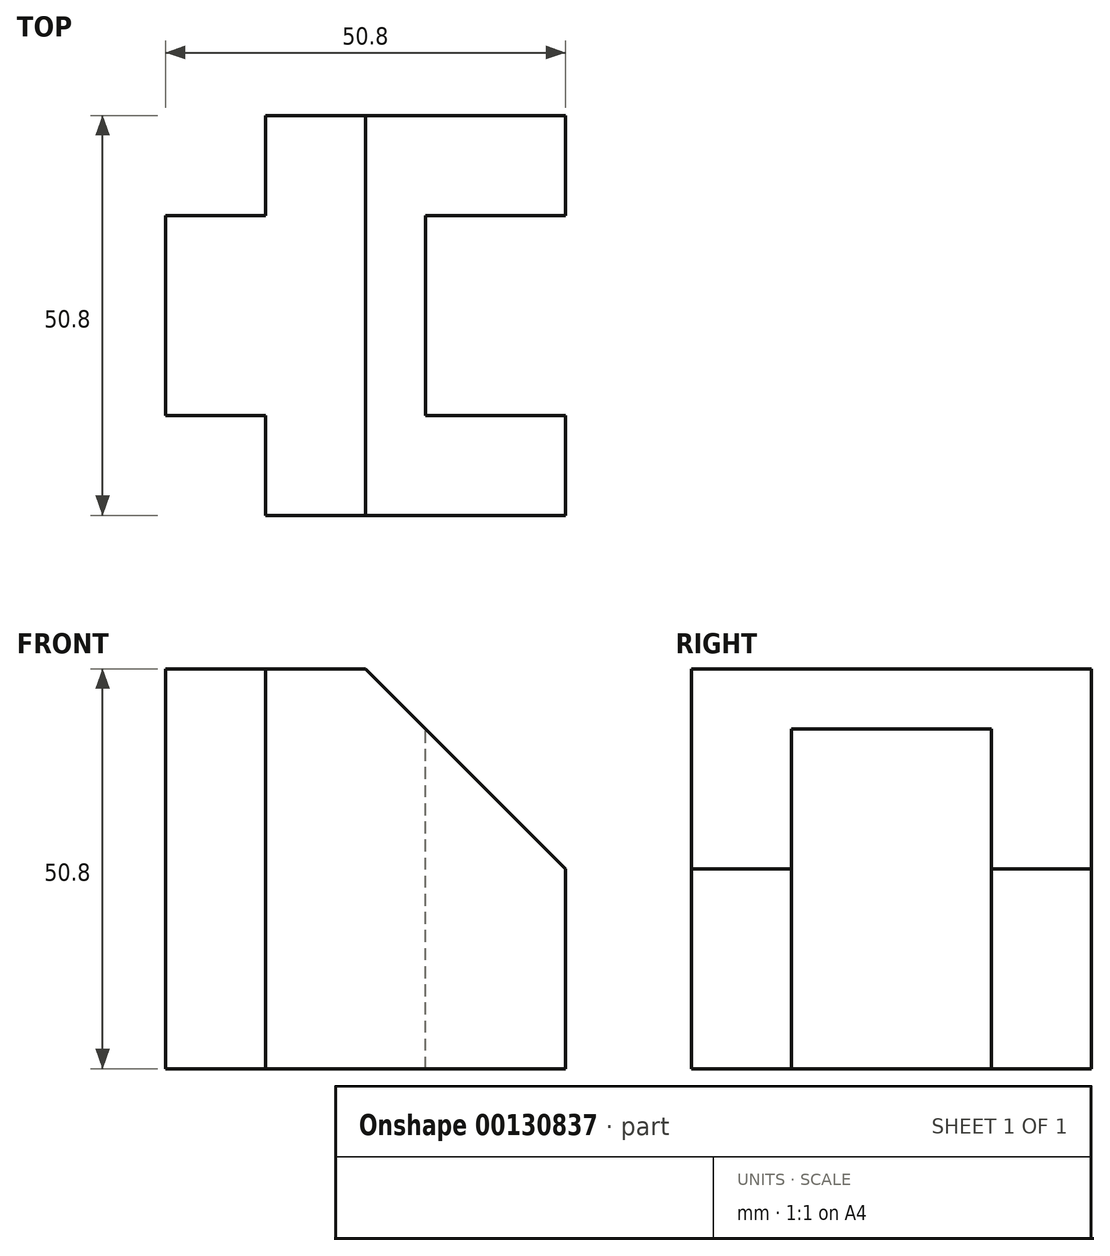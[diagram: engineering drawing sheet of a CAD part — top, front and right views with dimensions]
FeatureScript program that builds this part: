
annotation { "Feature Type Name" : "Feature", "Feature Type Description" : "" }
export const myFeature = defineFeature(function(context is Context, id is Id, definition is map)
    precondition{}
    {
        {
            var Q0;
            Q0=qCreatedBy(makeId("Front.planeOp"),FACE);
            var sketch = newSketch(context, id + "F0", { "sketchPlane" : qUnion([Q0])});
            skLineSegment(sketch, "E0", {"start": v(0, 0) * mm, "end": v(0, 50.8) * mm});
            skLineSegment(sketch, "E1", {"start": v(0, 50.8) * mm, "end": v(25.4, 50.8) * mm});
            skLineSegment(sketch, "E2", {"start": v(25.4, 50.8) * mm, "end": v(50.8, 25.4) * mm});
            skLineSegment(sketch, "E3", {"start": v(50.8, 25.4) * mm, "end": v(50.8, 0) * mm});
            skLineSegment(sketch, "E4", {"start": v(50.8, 0) * mm, "end": v(0, 0) * mm});
            skSolve(sketch);
        }
        {
            var Q0;
            Q0 = qSketchRegion(id + "F0", true);
            extrude(context, id + "F1", {"entities" : qUnion([Q0]), "oppositeDirection" : true, "depth" : 50.8 * mm});
        }
        {
            var Q0;
            Q0=makeQuery(id+"F1.opExtrude","SWEPT_FACE",FACE,{"disambiguationData":[OSD([sQuery(id+"F0.wireOp",EDGE,"E1")])]});
            var sketch = newSketch(context, id + "F2", { "sketchPlane" : qUnion([Q0])});
            skLineSegment(sketch, "E5", {"start": v(0, 50.8) * mm, "end": v(12.7, 50.8) * mm});
            skLineSegment(sketch, "E6", {"start": v(12.7, 50.8) * mm, "end": v(12.7, 38.1) * mm});
            skLineSegment(sketch, "E7", {"start": v(12.7, 38.1) * mm, "end": v(0, 38.1) * mm});
            skLineSegment(sketch, "E8", {"start": v(0, 38.1) * mm, "end": v(0, 50.8) * mm});
            skLineSegment(sketch, "E9", {"start": v(0, 0) * mm, "end": v(0, 12.7) * mm});
            skLineSegment(sketch, "E10", {"start": v(0, 12.7) * mm, "end": v(12.7, 12.7) * mm});
            skLineSegment(sketch, "E11", {"start": v(12.7, 12.7) * mm, "end": v(12.7, 0) * mm});
            skLineSegment(sketch, "E12", {"start": v(12.7, 0) * mm, "end": v(0, 0) * mm});
            skSolve(sketch);
        }
        {
            var Q0;
            Q0 = qSketchRegion(id + "F2", true);
            extrude(context, id + "F3", {"entities" : qUnion([Q0]), "operationType" : NewBodyOperationType.REMOVE, "endBound" : BoundingType.THROUGH_ALL, "oppositeDirection" : true, "depth" : 25.4 * mm});
        }
        {
            var Q0;
            Q0=makeQuery(id+"F1.opExtrude","SWEPT_FACE",FACE,{"disambiguationData":[OSD([sQuery(id+"F0.wireOp",EDGE,"E1")])]});
            var sketch = newSketch(context, id + "F4", { "sketchPlane" : qUnion([Q0])});
            skLineSegment(sketch, "E13.0", {"start": v(50.8, 50.8) * mm, "end": v(50.8, 0) * mm});
            skLineSegment(sketch, "E14.0.1", {"start": v(50.8, 12.7) * mm, "end": v(50.8, 38.1) * mm});
            skLineSegment(sketch, "E15", {"start": v(50.8, 38.1) * mm, "end": v(33.02, 38.1) * mm});
            skLineSegment(sketch, "E16", {"start": v(33.02, 38.1) * mm, "end": v(33.02, 12.7) * mm});
            skLineSegment(sketch, "E17", {"start": v(33.02, 12.7) * mm, "end": v(50.8, 12.7) * mm});
            skSolve(sketch);
        }
        {
            var Q0;
            Q0 = qSketchRegion(id + "F4", true);
            extrude(context, id + "F5", {"entities" : qUnion([Q0]), "operationType" : NewBodyOperationType.REMOVE, "endBound" : BoundingType.THROUGH_ALL, "oppositeDirection" : true, "depth" : 25.4 * mm});
        }
    });
